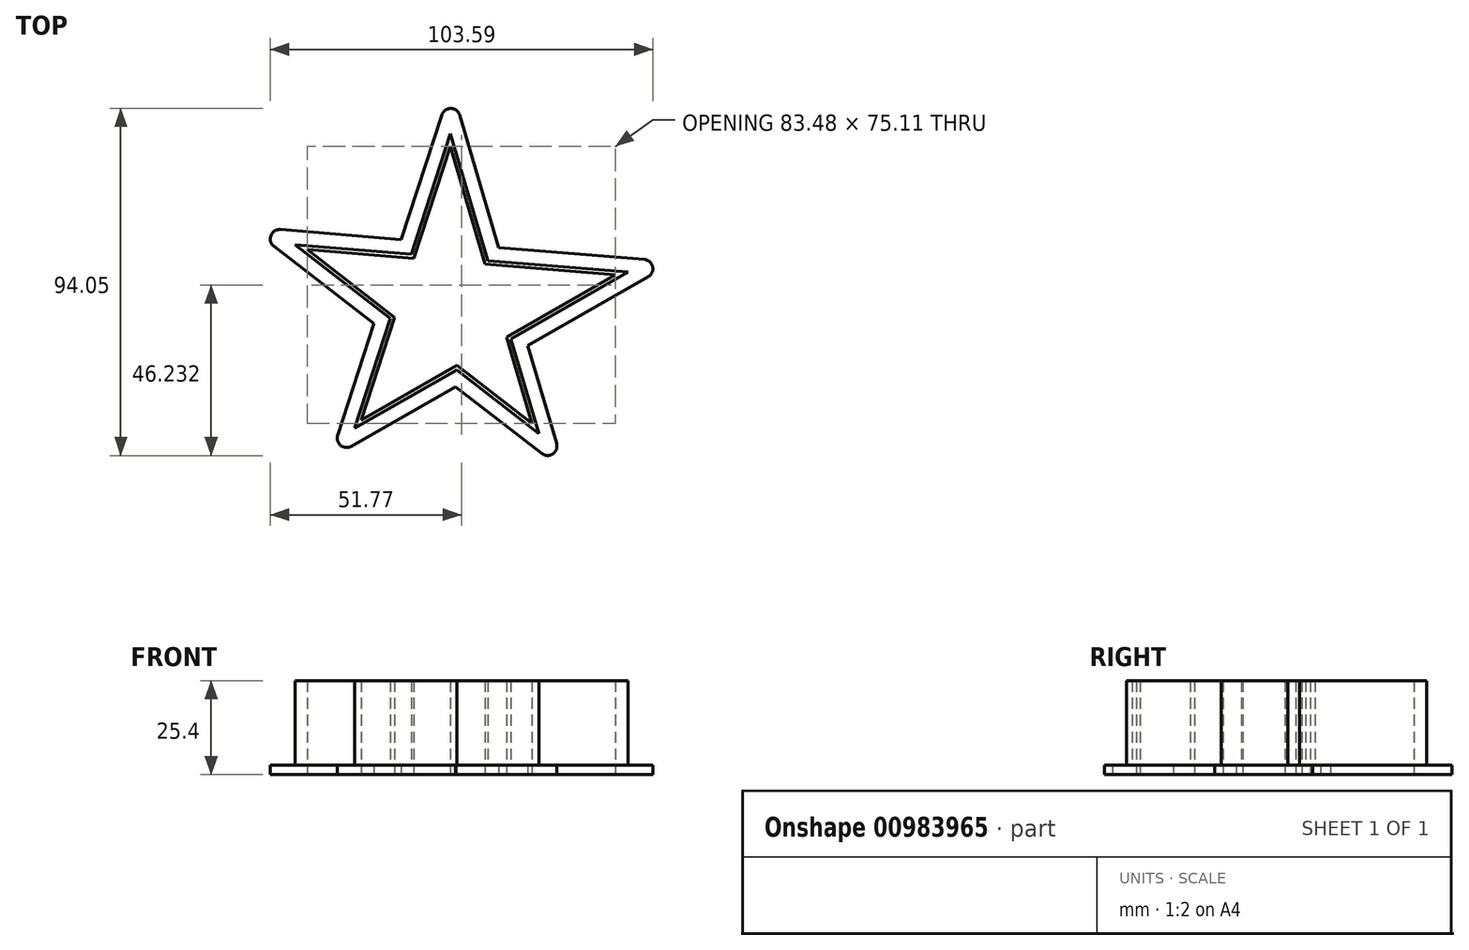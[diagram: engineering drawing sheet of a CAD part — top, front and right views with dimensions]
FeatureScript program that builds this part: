
annotation { "Feature Type Name" : "Feature", "Feature Type Description" : "" }
export const myFeature = defineFeature(function(context is Context, id is Id, definition is map)
    precondition{}
    {
        {
            var Q0;
            Q0=qCreatedBy(makeId("Top.planeOp"),FACE);
            var sketch = newSketch(context, id + "F0", { "sketchPlane" : qUnion([Q0])});
            skLineSegment(sketch, "E0", {"start": v(0.3, 40.8) * mm, "end": v(9.72, 8.86) * mm});
            skLineSegment(sketch, "E1", {"start": v(-23.79, -33.34) * mm, "end": v(-14.75, -5.5) * mm});
            skLineSegment(sketch, "E2", {"start": v(45.07, 5.96) * mm, "end": v(9.72, 8.86) * mm});
            skLineSegment(sketch, "E3", {"start": v(22.46, -34.3) * mm, "end": v(2.11, -18.55) * mm});
            skLineSegment(sketch, "E4", {"start": v(-23.79, -33.34) * mm, "end": v(2.11, -18.55) * mm});
            skLineSegment(sketch, "E5.trimOffspring", {"start": v(-9.56, 10.45) * mm, "end": v(-38.4, 12.81) * mm});
            skLineSegment(sketch, "E6.trimOffspring", {"start": v(15.55, -10.88) * mm, "end": v(22.46, -34.3) * mm});
            skLineSegment(sketch, "E7.trimOffspring", {"start": v(15.55, -10.88) * mm, "end": v(45.07, 5.96) * mm});
            skLineSegment(sketch, "E8.trimOffspring", {"start": v(-14.75, -5.5) * mm, "end": v(-38.4, 12.81) * mm});
            skLineSegment(sketch, "E9.trimOffspring", {"start": v(-9.56, 10.45) * mm, "end": v(0.3, 40.8) * mm});
            skLineSegment(sketch, "E10.0", {"start": v(21.26, -13.18) * mm, "end": v(53.87, 5.43) * mm});
            skLineSegment(sketch, "E10.1", {"start": v(21.26, -13.18) * mm, "end": v(29.1, -39.72) * mm});
            skLineSegment(sketch, "E10.2", {"start": v(52.82, 10.17) * mm, "end": v(13.42, 13.4) * mm});
            skLineSegment(sketch, "E10.3", {"start": v(25.1, -42.45) * mm, "end": v(1.7, -24.34) * mm});
            skLineSegment(sketch, "E10.4", {"start": v(-26.53, -40.46) * mm, "end": v(1.7, -24.34) * mm});
            skLineSegment(sketch, "E10.5", {"start": v(-30.2, -37.47) * mm, "end": v(-20.39, -7.24) * mm});
            skLineSegment(sketch, "E10.6", {"start": v(2.84, 49.25) * mm, "end": v(13.42, 13.4) * mm});
            skLineSegment(sketch, "E10.7", {"start": v(-12.97, 15.57) * mm, "end": v(-2.01, 49.31) * mm});
            skLineSegment(sketch, "E10.8", {"start": v(-12.97, 15.57) * mm, "end": v(-45.7, 18.25) * mm});
            skLineSegment(sketch, "E10.9", {"start": v(-20.39, -7.24) * mm, "end": v(-47.46, 13.71) * mm});
            skPoint(sketch, "E11.visualSharp", {"position": v(31.31, -47.26) * mm});
            skArc(sketch, "E11.filletArc", {"start": v(25.1, -42.45) * mm, "mid": v(28.09, -42.54) * mm, "end": v(29.1, -39.72) * mm});
            skPoint(sketch, "E12.visualSharp", {"position": v(61, 9.5) * mm});
            skArc(sketch, "E12.filletArc", {"start": v(53.87, 5.43) * mm, "mid": v(55.1, 8.19) * mm, "end": v(52.82, 10.17) * mm});
            skPoint(sketch, "E13.visualSharp", {"position": v(0.52, 57.1) * mm});
            skArc(sketch, "E13.filletArc", {"start": v(2.84, 49.25) * mm, "mid": v(0.44, 51.07) * mm, "end": v(-2.01, 49.31) * mm});
            skPoint(sketch, "E14.visualSharp", {"position": v(-54.23, 18.95) * mm});
            skArc(sketch, "E14.filletArc", {"start": v(-45.7, 18.25) * mm, "mid": v(-48.27, 16.64) * mm, "end": v(-47.46, 13.71) * mm});
            skPoint(sketch, "E15.visualSharp", {"position": v(-32.24, -43.71) * mm});
            skArc(sketch, "E15.filletArc", {"start": v(-30.2, -37.47) * mm, "mid": v(-29.4, -40.22) * mm, "end": v(-26.53, -40.46) * mm});
            skLineSegment(sketch, "E16.0", {"start": v(-10.28, 11.52) * mm, "end": v(0.35, 44.24) * mm});
            skLineSegment(sketch, "E16.1", {"start": v(0.35, 44.24) * mm, "end": v(10.5, 9.82) * mm});
            skLineSegment(sketch, "E16.2", {"start": v(-10.28, 11.52) * mm, "end": v(-41.74, 14.1) * mm});
            skLineSegment(sketch, "E16.3", {"start": v(48.42, 6.7) * mm, "end": v(10.5, 9.82) * mm});
            skLineSegment(sketch, "E16.4", {"start": v(16.75, -11.37) * mm, "end": v(48.42, 6.7) * mm});
            skLineSegment(sketch, "E16.5", {"start": v(16.75, -11.37) * mm, "end": v(24.32, -37.03) * mm});
            skLineSegment(sketch, "E16.6", {"start": v(-15.93, -5.87) * mm, "end": v(-41.74, 14.1) * mm});
            skLineSegment(sketch, "E16.7", {"start": v(-25.57, -35.52) * mm, "end": v(-15.93, -5.87) * mm});
            skLineSegment(sketch, "E16.8", {"start": v(-25.57, -35.52) * mm, "end": v(2.03, -19.77) * mm});
            skLineSegment(sketch, "E16.9", {"start": v(24.32, -37.03) * mm, "end": v(2.03, -19.77) * mm});
            skSolve(sketch);
        }
        {
            var Q0;
            Q0=makeQuery(id+"F0.imprint","IMPRINT",FACE,{"disambiguationData":[TD([[makeQuery(id+"F0.imprint","IMPRINT",EDGE,{"derivedFrom":sQuery(id+"F0.wireOp",EDGE,"E0")}),1.0]])]});
            extrude(context, id + "F1", {"entities" : qUnion([Q0]), "depth" : 25.4 * mm, "offsetDistance" : 25.4 * mm});
        }
        {
            var Q0;
            Q0=makeQuery(id+"F0.imprint","IMPRINT",FACE,{"disambiguationData":[TD([[makeQuery(id+"F0.imprint","IMPRINT",EDGE,{"derivedFrom":sQuery(id+"F0.wireOp",EDGE,"E10.0")}),1.0]])]});
            extrude(context, id + "F2", {"entities" : qUnion([Q0]), "operationType" : NewBodyOperationType.ADD, "depth" : 2.54 * mm, "offsetDistance" : 25.4 * mm});
        }
    });
